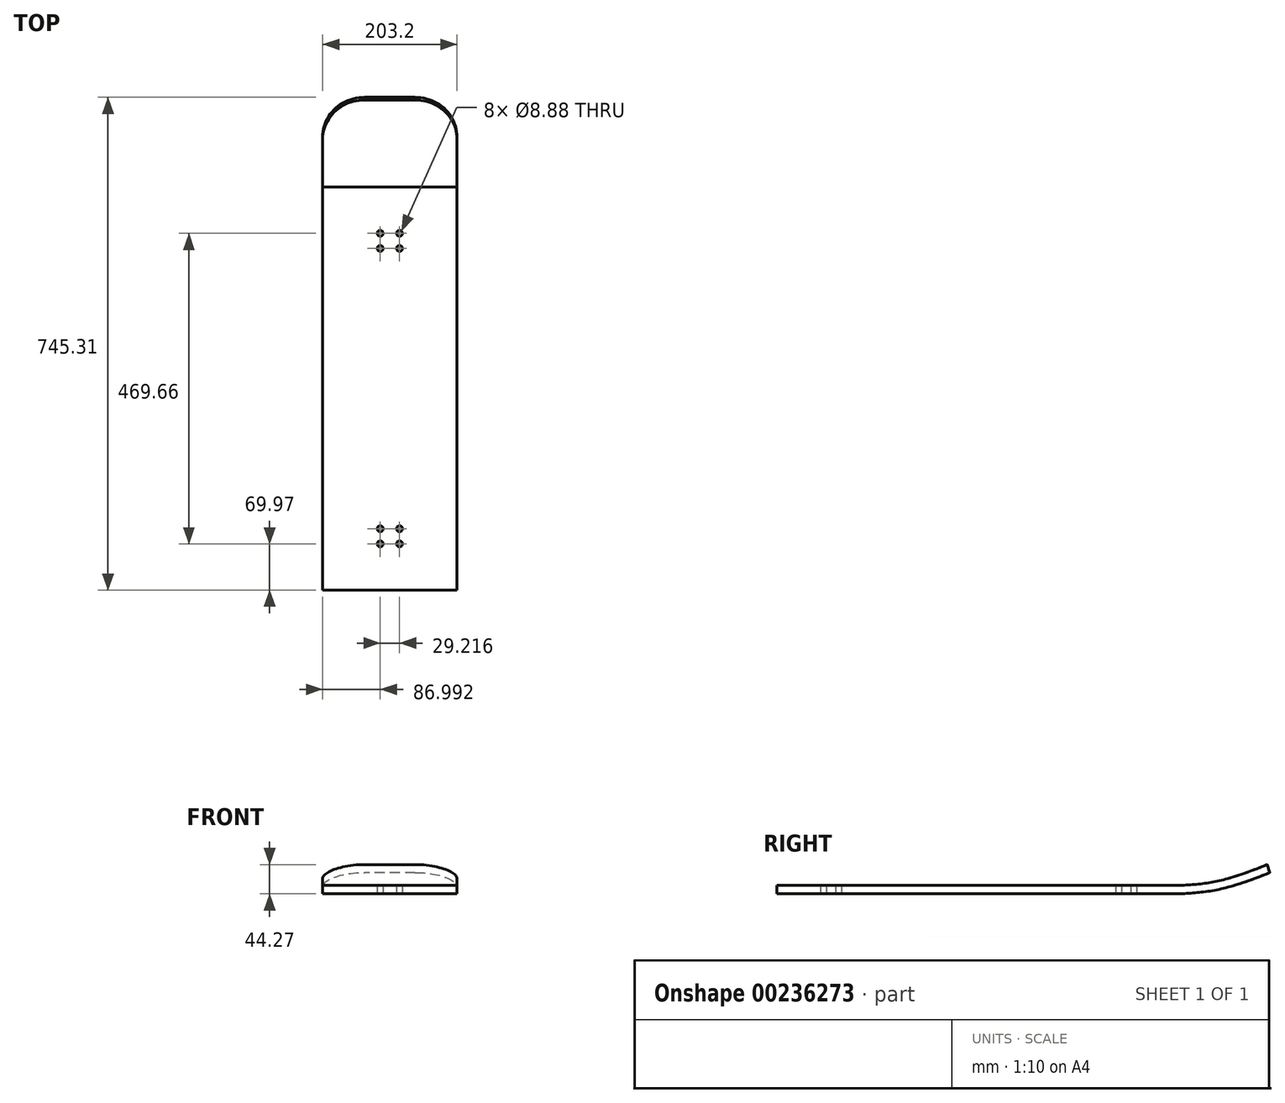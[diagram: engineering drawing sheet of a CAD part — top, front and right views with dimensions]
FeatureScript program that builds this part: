
annotation { "Feature Type Name" : "Feature", "Feature Type Description" : "" }
export const myFeature = defineFeature(function(context is Context, id is Id, definition is map)
    precondition{}
    {
        {
            var Q0;
            Q0=qCreatedBy(makeId("Top.planeOp"),FACE);
            var sketch = newSketch(context, id + "F0", { "sketchPlane" : qUnion([Q0])});
            skLineSegment(sketch, "E0.bottom", {"start": v(101.6, -304.8) * mm, "end": v(-101.6, -304.8) * mm});
            skLineSegment(sketch, "E0.top", {"start": v(101.6, 304.8) * mm, "end": v(-101.6, 304.8) * mm});
            skLineSegment(sketch, "E0.left", {"start": v(101.6, -304.8) * mm, "end": v(101.6, 304.8) * mm});
            skLineSegment(sketch, "E0.right", {"start": v(-101.6, -304.8) * mm, "end": v(-101.6, 304.8) * mm});
            skPoint(sketch, "E0.middle", {"position": v(0, 0) * mm});
            skPoint(sketch, "E1.middle", {"position": v(0, 223.4) * mm});
            skCircle(sketch, "E2", {"center": v(-14.6, 234.83) * mm, "radius": 4.44 * mm});
            skCircle(sketch, "E3", {"center": v(14.6, 234.83) * mm, "radius": 4.44 * mm});
            skCircle(sketch, "E4", {"center": v(-14.6, 211.96) * mm, "radius": 4.44 * mm});
            skCircle(sketch, "E5", {"center": v(14.6, 211.96) * mm, "radius": 4.44 * mm});
            skPoint(sketch, "E1.right.end.orphan", {"position": v(-25.4, 248.8) * mm});
            skPoint(sketch, "E1.left.end.orphan", {"position": v(25.4, 248.8) * mm});
            skPoint(sketch, "E1.bottom.end.orphan", {"position": v(-25.4, 198) * mm});
            skPoint(sketch, "E1.bottom.start.orphan", {"position": v(25.4, 198) * mm});
            skCircle(sketch, "E6.MirrorC", {"center": v(-14.6, -234.83) * mm, "radius": 4.44 * mm});
            skCircle(sketch, "E7.MirrorC", {"center": v(14.6, -234.83) * mm, "radius": 4.44 * mm});
            skCircle(sketch, "E8.MirrorC", {"center": v(14.6, -211.96) * mm, "radius": 4.44 * mm});
            skCircle(sketch, "E9.MirrorC", {"center": v(-14.6, -211.96) * mm, "radius": 4.44 * mm});
            skSolve(sketch);
        }
        {
            var Q0;
            Q0 = qSketchRegion(id + "F0", true);
            extrude(context, id + "F1", {"entities" : qUnion([Q0]), "endBound" : BoundingType.SYMMETRIC, "depth" : 12.7 * mm});
        }
        {
            var Q0;
            Q0=qCreatedBy(makeId("Right.planeOp"),FACE);
            var sketch = newSketch(context, id + "F2", { "sketchPlane" : qUnion([Q0])});
            skFitSpline(sketch, "E10", {"points": [v(304.7, 0) * mm, v(356.86, 5.52) * mm, v(408.41, 20.25) * mm, v(438.48, 31.91) * mm], "startDerivative": vector(144.02, 8.74) * mm, "endDerivative": vector(99.08, 40.27) * mm});
            skFitSpline(sketch, "E11", {"points": [v(-304.68, 0) * mm, v(-341.34, 0) * mm, v(-386.24, 9.73) * mm, v(-420.66, 23.94) * mm], "startDerivative": vector(-110.68, -5.76) * mm, "endDerivative": vector(-101.34, 46.6) * mm});
            skSolve(sketch);
        }
        {
            var Q0;
            Q0=makeQuery(id+"F1.opExtrude","SWEPT_FACE",FACE,{"disambiguationData":[OSD([sQuery(id+"F0.wireOp",EDGE,"E0.top")])]});
            var Q1;
            Q1=sQuery(id+"F2.wireOp",EDGE,"E10");
            sweep(context, id + "F3", {"operationType" : NewBodyOperationType.ADD, "profiles" : qUnion([Q0]), "path" : qUnion([Q1])});
        }
        {
            var Q0;
            Q0=makeQuery(id+"F3.opSweep","CAP_EDGE",EDGE,{"disambiguationData":[OSD([sQuery(id+"F0.wireOp",EDGE,"E0.top"),sQuery(id+"F0.wireOp",EDGE,"E0.left"),sQuery(id+"F2.wireOp",VERTEX,"E10.end")])],"isStart":false});
            var Q1;
            Q1=makeQuery(id+"F3.opSweep","CAP_EDGE",EDGE,{"disambiguationData":[OSD([sQuery(id+"F0.wireOp",EDGE,"E0.top"),sQuery(id+"F0.wireOp",EDGE,"E0.right"),sQuery(id+"F2.wireOp",VERTEX,"E10.end")])],"isStart":false});
            fillet(context, id + "F4", {"entities" : qUnion([Q0, Q1]), "radius" : 63.5 * mm, "tangentPropagation" : true, "allowEdgeOverflow" : false});
        }
    });
